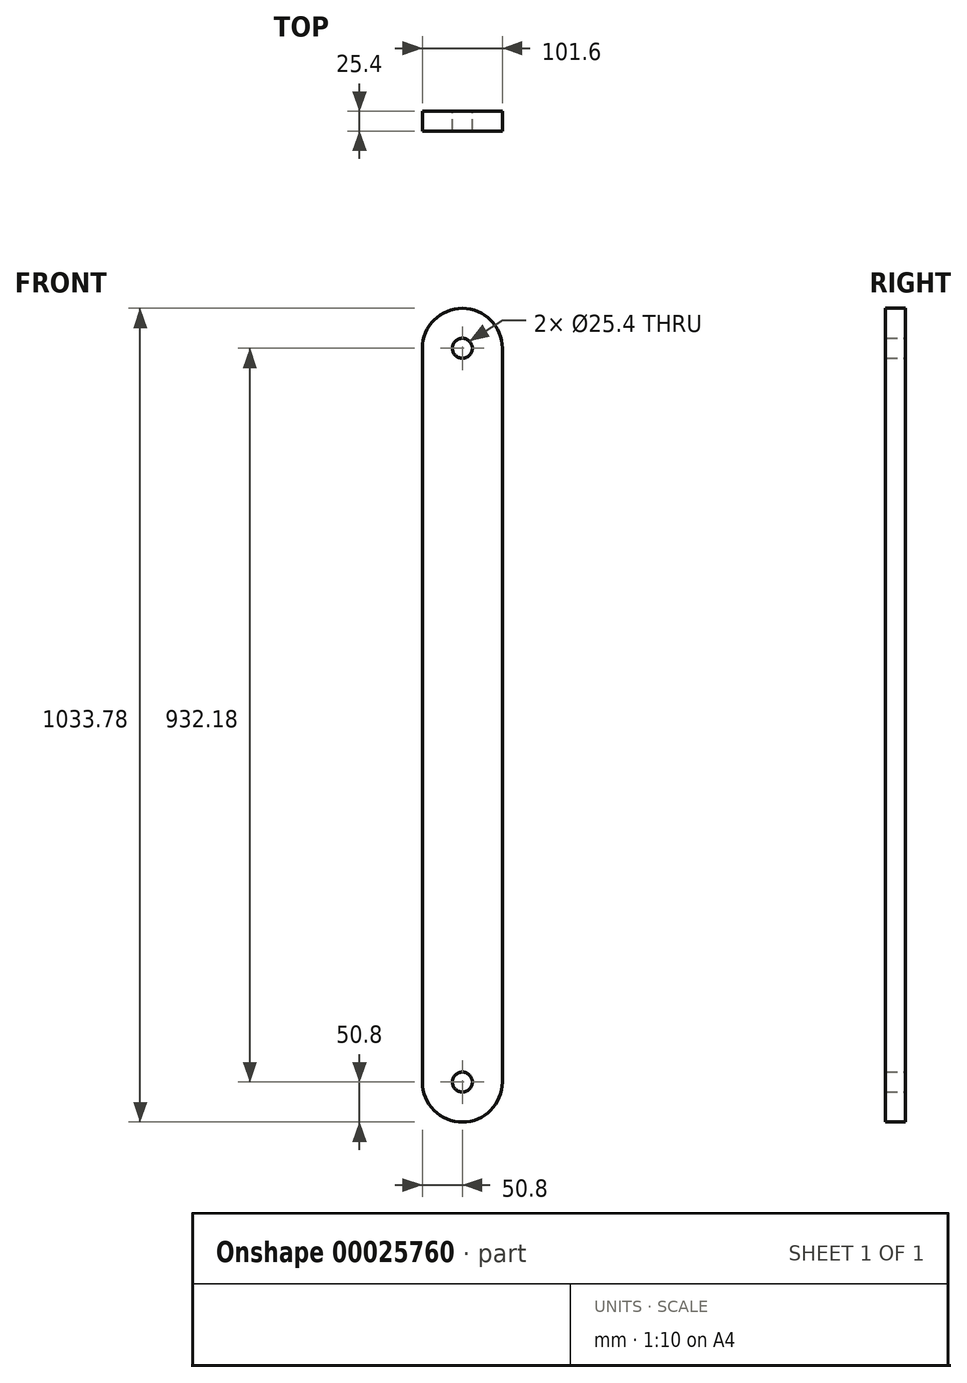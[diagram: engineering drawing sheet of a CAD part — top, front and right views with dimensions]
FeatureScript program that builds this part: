
annotation { "Feature Type Name" : "Feature", "Feature Type Description" : "" }
export const myFeature = defineFeature(function(context is Context, id is Id, definition is map)
    precondition{}
    {
        {
            var Q0;
            Q0=qCreatedBy(makeId("Front.planeOp"),FACE);
            var sketch = newSketch(context, id + "F0", { "sketchPlane" : qUnion([Q0])});
            skCircle(sketch, "E0", {"center": v(0, 0) * mm, "radius": 12.7 * mm});
            skLineSegment(sketch, "E1", {"start": v(50.8, 0) * mm, "end": v(50.8, 932.18) * mm});
            skLineSegment(sketch, "E2", {"start": v(-50.8, 0) * mm, "end": v(-50.8, 932.18) * mm});
            skArc(sketch, "E3", {"start": v(-50.8, 0) * mm, "mid": v(0, -50.8) * mm, "end": v(50.8, 0) * mm});
            skArc(sketch, "E4", {"start": v(50.8, 932.18) * mm, "mid": v(0, 982.98) * mm, "end": v(-50.8, 932.18) * mm});
            skCircle(sketch, "E5", {"center": v(0, 932.18) * mm, "radius": 12.7 * mm});
            skSolve(sketch);
        }
        {
            var Q0;
            Q0=qSketchRegion(id+"F0",true);
            extrude(context, id + "F1", {"entities" : qUnion([Q0]), "depth" : 25.4 * mm});
        }
    });
